# Revit family: 1QF_MACOM_FL92C-DA_In-line Cooker_EN
name_source: partatom
category: Specialty Equipment
units: mm (PartAtom-declared; Revit-internal decimal feet)

## family parameters
Always vertical = Yes
Cut with Voids When Loaded = No
OmniClass Number = 23.40.40.14.17.11
OmniClass Title = Cookers, Ovens, Stoves
Part Type = Normal
Room Calculation Point = No
Round Connector Dimension = Use Diameter
Shared = No
Work Plane-Based = No

## types (2) — shared parameters
Assembly Code = E1090320
CSI MasterFormat = 11 44 13
Capacity = 0.0 L
Depth Actual = 572 mm
Gas Pressure = 0.0 bar
Height Actual = 245 mm  [stored 0.803806 ft]
Length Actual = 900 mm  [stored 2.95276 ft]
Manufacturer = MACOM
Number of Burners = 2
URL = https://www.acosmacom.com.br
Volume = 0.13 m³
Weight = 65.00 kg
Work Temperature = -
zero-valued in all types: Default Elevation

## per-type parameters (varying)
| type | Description | Gas Flow | Gas Input |
| FL92C-G | FOGAO EM LINHA DE ENCOSTO A GAS GLP 900HP COM 02 QUEIMADORES | 0.5 m³/h | 59425 Btu/h |
| FL92C-N | FOGAO EM LINHA DE ENCOSTO A GAS NATURAL 900HP COM 02 QUEIMADORES | 1.6 m³/h | 59430 Btu/h |

note: column(s) folded — value = type name in every type: Model

note: [stored X ft] marks values corroborated as IEEE doubles in the binary element streams (Revit-internal decimal feet)

## geometry (parser evidence)
native form markers: Sweep x10
no freeform markers — native parametric forms only
